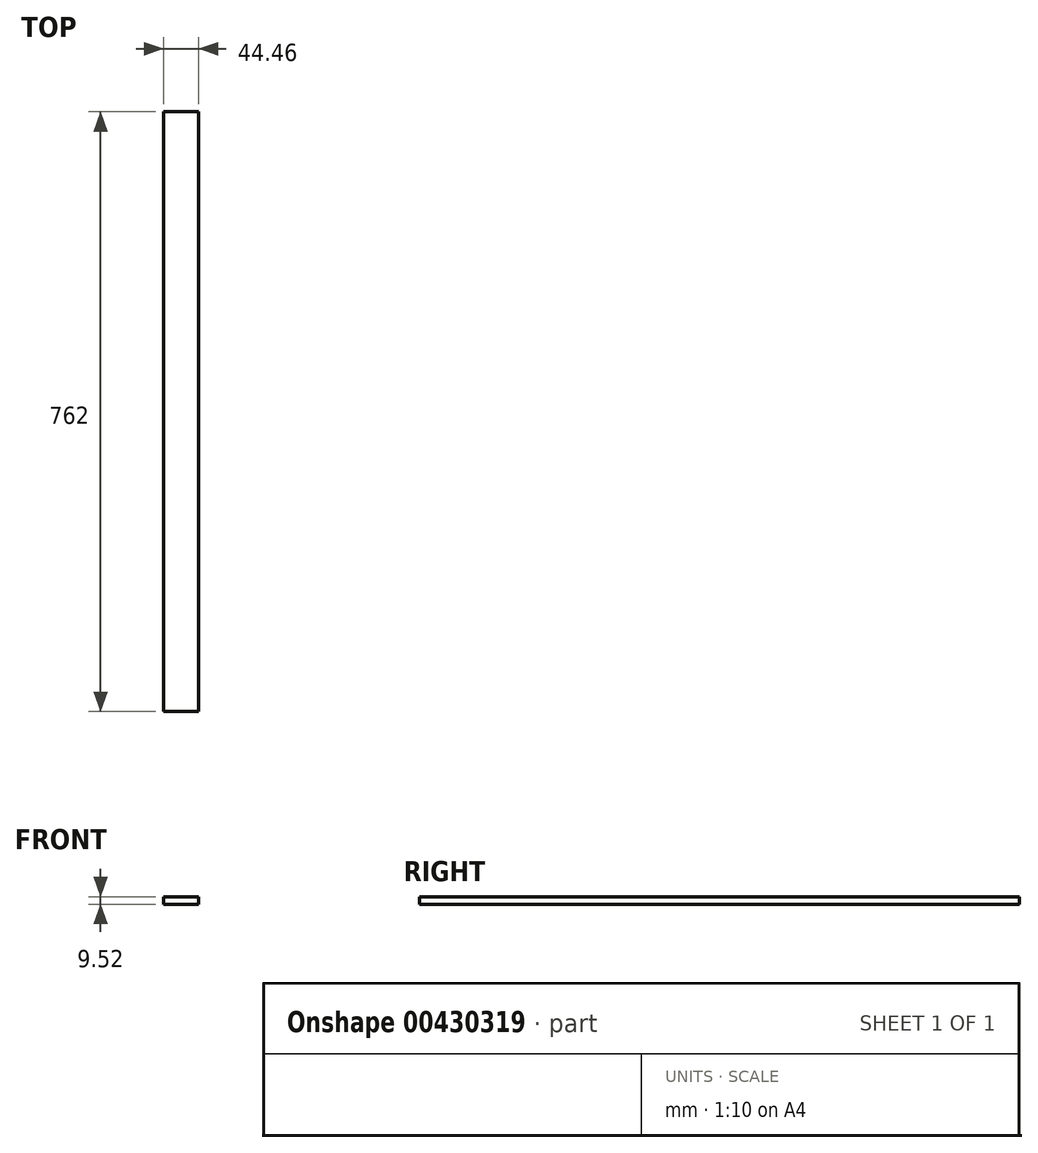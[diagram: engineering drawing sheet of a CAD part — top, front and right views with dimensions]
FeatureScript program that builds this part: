
annotation { "Feature Type Name" : "Feature", "Feature Type Description" : "" }
export const myFeature = defineFeature(function(context is Context, id is Id, definition is map)
    precondition{}
    {
        {
            var Q0;
            Q0=qCreatedBy(makeId("Front.planeOp"),FACE);
            var sketch = newSketch(context, id + "F0", { "sketchPlane" : qUnion([Q0])});
            skLineSegment(sketch, "E0.bottom", {"start": v(22.22, 4.76) * mm, "end": v(-22.23, 4.76) * mm});
            skLineSegment(sketch, "E0.top", {"start": v(22.22, -4.76) * mm, "end": v(-22.23, -4.76) * mm});
            skLineSegment(sketch, "E0.left", {"start": v(22.23, 4.76) * mm, "end": v(22.23, -4.76) * mm});
            skLineSegment(sketch, "E0.right", {"start": v(-22.23, 4.76) * mm, "end": v(-22.23, -4.76) * mm});
            skPoint(sketch, "E0.middle", {"position": v(0, 0) * mm});
            skSolve(sketch);
        }
        {
            var Q0;
            Q0=makeQuery(id+"F0.imprint","IMPRINT",FACE,{"disambiguationData":[TD([[makeQuery(id+"F0.imprint","IMPRINT",EDGE,{"derivedFrom":sQuery(id+"F0.wireOp",EDGE,"E0.bottom")}),1.0]])]});
            extrude(context, id + "F1", {"entities" : qUnion([Q0]), "depth" : 762 * mm});
        }
    });
